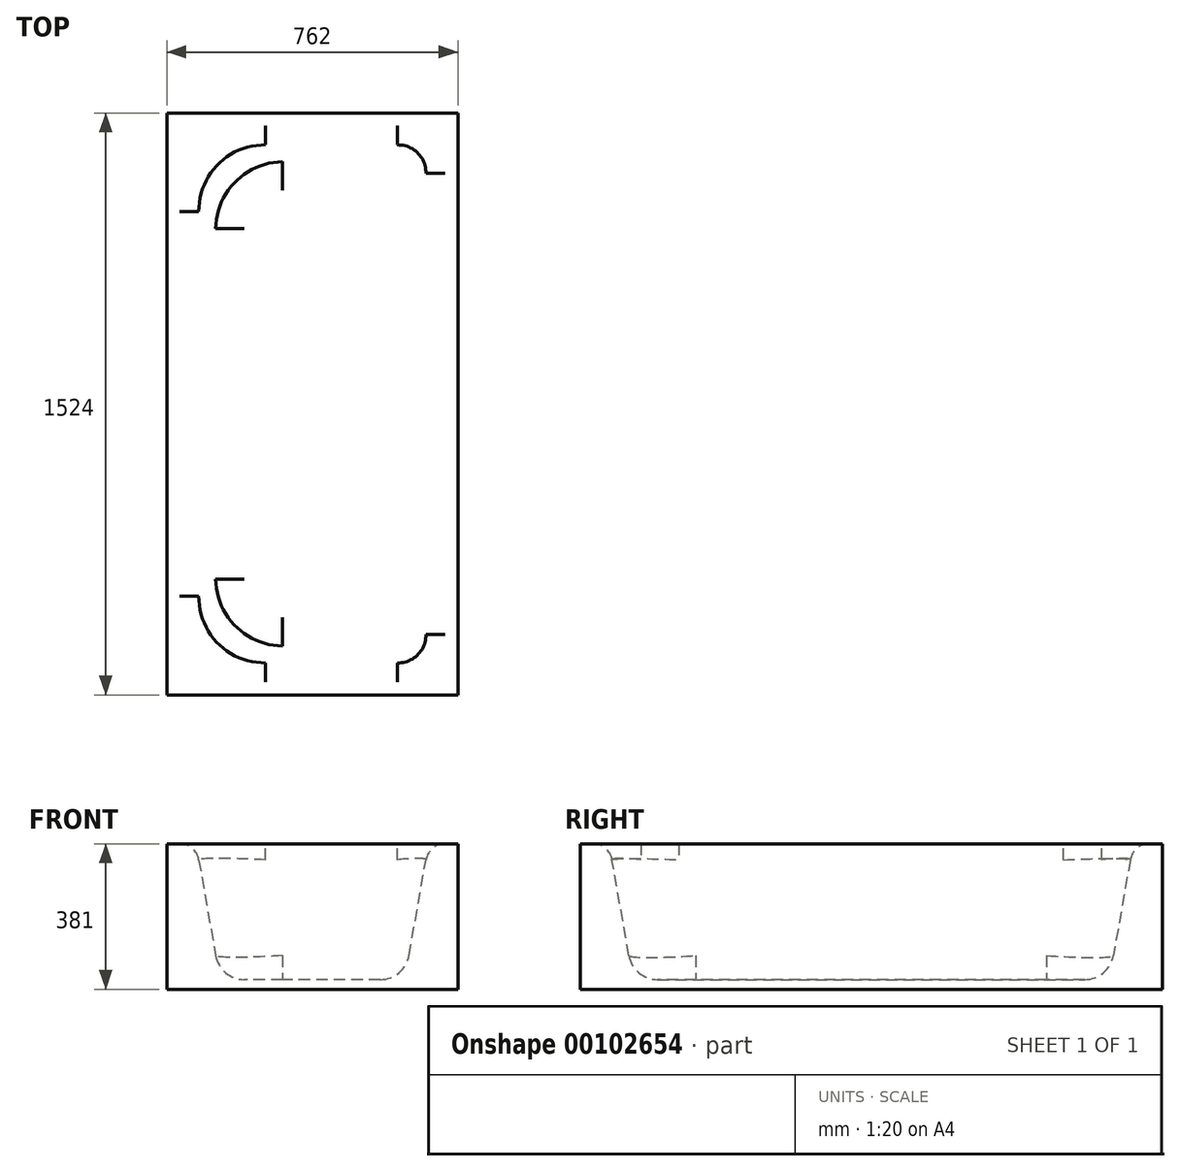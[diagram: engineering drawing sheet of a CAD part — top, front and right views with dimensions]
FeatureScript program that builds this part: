
annotation { "Feature Type Name" : "Feature", "Feature Type Description" : "" }
export const myFeature = defineFeature(function(context is Context, id is Id, definition is map)
    precondition{}
    {
        {
            var Q0;
            Q0=qCreatedBy(makeId("Top.planeOp"),FACE);
            var sketch = newSketch(context, id + "F0", { "sketchPlane" : qUnion([Q0])});
            skLineSegment(sketch, "E0.bottom", {"start": v(0, 0) * mm, "end": v(762, 0) * mm});
            skLineSegment(sketch, "E0.top", {"start": v(0, 1524) * mm, "end": v(762, 1524) * mm});
            skLineSegment(sketch, "E0.left", {"start": v(0, 0) * mm, "end": v(0, 1524) * mm});
            skLineSegment(sketch, "E0.right", {"start": v(762, 0) * mm, "end": v(762, 1524) * mm});
            skSolve(sketch);
        }
        {
            var Q0;
            Q0 = qSketchRegion(id + "F0", true);
            extrude(context, id + "F1", {"entities" : qUnion([Q0]), "depth" : 381 * mm});
        }
        {
            var Q0;
            Q0=makeQuery(id+"F1.opExtrude","CAP_FACE",FACE,{"disambiguationData":[OSD([sQuery(id+"F0.wireOp",EDGE,"E0.bottom"),sQuery(id+"F0.wireOp",EDGE,"E0.top"),sQuery(id+"F0.wireOp",EDGE,"E0.left"),sQuery(id+"F0.wireOp",EDGE,"E0.right")])],"isStart":false});
            var sketch = newSketch(context, id + "F2", { "sketchPlane" : qUnion([Q0])});
            skLineSegment(sketch, "E1.bottom", {"start": v(76.2, 1447.8) * mm, "end": v(685.8, 1447.8) * mm});
            skLineSegment(sketch, "E1.top", {"start": v(76.2, 76.2) * mm, "end": v(685.8, 76.2) * mm});
            skLineSegment(sketch, "E1.left", {"start": v(76.2, 1447.8) * mm, "end": v(76.2, 76.2) * mm});
            skLineSegment(sketch, "E1.right", {"start": v(685.8, 1447.8) * mm, "end": v(685.8, 76.2) * mm});
            skSolve(sketch);
        }
        {
            var Q0;
            Q0 = qSketchRegion(id + "F2", true);
            extrude(context, id + "F3", {"entities" : qUnion([Q0]), "operationType" : NewBodyOperationType.REMOVE, "oppositeDirection" : true, "depth" : 355.6 * mm, "hasDraft" : true, "draftAngle" : 10 * degree, "draftPullDirection" : true});
        }
        {
            var Q0;
            Q0=makeQuery(id+"F3.boolean.opBoolean","COPY",EDGE,{"derivedFrom":makeQuery(id+"F3.opExtrude","SWEPT_EDGE",EDGE,{"disambiguationData":[OSD([sQuery(id+"F2.wireOp",EDGE,"E1.bottom"),sQuery(id+"F2.wireOp",EDGE,"E1.left")])]})});
            var Q1;
            Q1=makeQuery(id+"F3.boolean.opBoolean","COPY",EDGE,{"derivedFrom":makeQuery(id+"F3.opExtrude","SWEPT_EDGE",EDGE,{"disambiguationData":[OSD([sQuery(id+"F2.wireOp",EDGE,"E1.top"),sQuery(id+"F2.wireOp",EDGE,"E1.left")])]})});
            fillet(context, id + "F4", {"entities" : qUnion([Q0, Q1]), "radius" : 177.8 * mm, "tangentPropagation" : true, "allowEdgeOverflow" : false});
        }
        {
            var Q0;
            Q0=makeQuery(id+"F3.boolean.opBoolean","COPY",EDGE,{"derivedFrom":makeQuery(id+"F3.opExtrude","SWEPT_EDGE",EDGE,{"disambiguationData":[OSD([sQuery(id+"F2.wireOp",EDGE,"E1.bottom"),sQuery(id+"F2.wireOp",EDGE,"E1.right")])]})});
            var Q1;
            Q1=makeQuery(id+"F3.boolean.opBoolean","COPY",EDGE,{"derivedFrom":makeQuery(id+"F3.opExtrude","SWEPT_EDGE",EDGE,{"disambiguationData":[OSD([sQuery(id+"F2.wireOp",EDGE,"E1.top"),sQuery(id+"F2.wireOp",EDGE,"E1.right")])]})});
            fillet(context, id + "F5", {"entities" : qUnion([Q0, Q1]), "radius" : 76.2 * mm, "tangentPropagation" : true, "allowEdgeOverflow" : false});
        }
        {
            var Q0;
            {var subQ0=sQuery(id+"F2.wireOp",EDGE,"E1.left");var subQ1=sQuery(id+"F2.wireOp",EDGE,"E1.bottom");Q0=makeQuery(id+"F4.opFillet","BLEND_EDGE",EDGE,{"blendedFrom":[makeQuery(id+"F3.boolean.opBoolean","COPY",EDGE,{"derivedFrom":makeQuery(id+"F3.opExtrude","SWEPT_EDGE",EDGE,{"disambiguationData":[OSD([subQ1,subQ0])]})}),makeQuery(id+"F3.boolean.opBoolean","COPY",FACE,{"derivedFrom":makeQuery(id+"F3.opExtrude","CAP_FACE",FACE,{"disambiguationData":[OSD([subQ1,sQuery(id+"F2.wireOp",EDGE,"E1.top"),subQ0,sQuery(id+"F2.wireOp",EDGE,"E1.right")])],"isStart":false})})],"blendedInto":[makeQuery(id+"F3.boolean.opBoolean","COPY",FACE,{"derivedFrom":makeQuery(id+"F3.opExtrude","CAP_FACE",FACE,{"disambiguationData":[OSD([subQ1,sQuery(id+"F2.wireOp",EDGE,"E1.top"),subQ0,sQuery(id+"F2.wireOp",EDGE,"E1.right")])],"isStart":false})})]});}
            var Q1;
            Q1=makeQuery(id+"F3.boolean.opBoolean","COPY",EDGE,{"derivedFrom":makeQuery(id+"F3.opExtrude","CAP_EDGE",EDGE,{"disambiguationData":[OSD([sQuery(id+"F2.wireOp",EDGE,"E1.bottom")])],"isStart":false})});
            var Q2;
            {var subQ0=sQuery(id+"F2.wireOp",EDGE,"E1.right");var subQ1=sQuery(id+"F2.wireOp",EDGE,"E1.bottom");Q2=makeQuery(id+"F5.opFillet","BLEND_EDGE",EDGE,{"blendedFrom":[makeQuery(id+"F3.boolean.opBoolean","COPY",EDGE,{"derivedFrom":makeQuery(id+"F3.opExtrude","SWEPT_EDGE",EDGE,{"disambiguationData":[OSD([subQ1,subQ0])]})}),makeQuery(id+"F3.boolean.opBoolean","COPY",FACE,{"derivedFrom":makeQuery(id+"F3.opExtrude","CAP_FACE",FACE,{"disambiguationData":[OSD([subQ1,sQuery(id+"F2.wireOp",EDGE,"E1.top"),sQuery(id+"F2.wireOp",EDGE,"E1.left"),subQ0])],"isStart":false})})],"blendedInto":[makeQuery(id+"F3.boolean.opBoolean","COPY",FACE,{"derivedFrom":makeQuery(id+"F3.opExtrude","CAP_FACE",FACE,{"disambiguationData":[OSD([subQ1,sQuery(id+"F2.wireOp",EDGE,"E1.top"),sQuery(id+"F2.wireOp",EDGE,"E1.left"),subQ0])],"isStart":false})})]});}
            var Q3;
            {var subQ0=sQuery(id+"F2.wireOp",EDGE,"E1.right");var subQ1=sQuery(id+"F2.wireOp",EDGE,"E1.top");Q3=makeQuery(id+"F5.opFillet","BLEND_EDGE",EDGE,{"blendedFrom":[makeQuery(id+"F3.boolean.opBoolean","COPY",EDGE,{"derivedFrom":makeQuery(id+"F3.opExtrude","SWEPT_EDGE",EDGE,{"disambiguationData":[OSD([subQ1,subQ0])]})}),makeQuery(id+"F3.boolean.opBoolean","COPY",FACE,{"derivedFrom":makeQuery(id+"F3.opExtrude","CAP_FACE",FACE,{"disambiguationData":[OSD([sQuery(id+"F2.wireOp",EDGE,"E1.bottom"),subQ1,sQuery(id+"F2.wireOp",EDGE,"E1.left"),subQ0])],"isStart":false})})],"blendedInto":[makeQuery(id+"F3.boolean.opBoolean","COPY",FACE,{"derivedFrom":makeQuery(id+"F3.opExtrude","CAP_FACE",FACE,{"disambiguationData":[OSD([sQuery(id+"F2.wireOp",EDGE,"E1.bottom"),subQ1,sQuery(id+"F2.wireOp",EDGE,"E1.left"),subQ0])],"isStart":false})})]});}
            var Q4;
            Q4=makeQuery(id+"F3.boolean.opBoolean","COPY",EDGE,{"derivedFrom":makeQuery(id+"F3.opExtrude","CAP_EDGE",EDGE,{"disambiguationData":[OSD([sQuery(id+"F2.wireOp",EDGE,"E1.top")])],"isStart":false})});
            var Q5;
            {var subQ0=sQuery(id+"F2.wireOp",EDGE,"E1.left");var subQ1=sQuery(id+"F2.wireOp",EDGE,"E1.top");Q5=makeQuery(id+"F4.opFillet","BLEND_EDGE",EDGE,{"blendedFrom":[makeQuery(id+"F3.boolean.opBoolean","COPY",EDGE,{"derivedFrom":makeQuery(id+"F3.opExtrude","SWEPT_EDGE",EDGE,{"disambiguationData":[OSD([subQ1,subQ0])]})}),makeQuery(id+"F3.boolean.opBoolean","COPY",FACE,{"derivedFrom":makeQuery(id+"F3.opExtrude","CAP_FACE",FACE,{"disambiguationData":[OSD([sQuery(id+"F2.wireOp",EDGE,"E1.bottom"),subQ1,subQ0,sQuery(id+"F2.wireOp",EDGE,"E1.right")])],"isStart":false})})],"blendedInto":[makeQuery(id+"F3.boolean.opBoolean","COPY",FACE,{"derivedFrom":makeQuery(id+"F3.opExtrude","CAP_FACE",FACE,{"disambiguationData":[OSD([sQuery(id+"F2.wireOp",EDGE,"E1.bottom"),subQ1,subQ0,sQuery(id+"F2.wireOp",EDGE,"E1.right")])],"isStart":false})})]});}
            var Q6;
            Q6=makeQuery(id+"F3.boolean.opBoolean","COPY",EDGE,{"derivedFrom":makeQuery(id+"F3.opExtrude","CAP_EDGE",EDGE,{"disambiguationData":[OSD([sQuery(id+"F2.wireOp",EDGE,"E1.left")])],"isStart":false})});
            var Q7;
            Q7=makeQuery(id+"F3.boolean.opBoolean","COPY",EDGE,{"derivedFrom":makeQuery(id+"F3.opExtrude","CAP_EDGE",EDGE,{"disambiguationData":[OSD([sQuery(id+"F2.wireOp",EDGE,"E1.right")])],"isStart":false})});
            fillet(context, id + "F6", {"entities" : qUnion([Q0, Q1, Q2, Q3, Q4, Q5, Q6, Q7]), "radius" : 76.2 * mm, "tangentPropagation" : true, "allowEdgeOverflow" : false});
        }
        {
            var Q0;
            Q0=makeQuery(id+"F4.opFillet","BLEND_EDGE",EDGE,{"blendedFrom":[makeQuery(id+"F3.boolean.opBoolean","COPY",EDGE,{"derivedFrom":makeQuery(id+"F3.opExtrude","SWEPT_EDGE",EDGE,{"disambiguationData":[OSD([sQuery(id+"F2.wireOp",EDGE,"E1.bottom"),sQuery(id+"F2.wireOp",EDGE,"E1.left")])]})}),makeQuery(id+"F1.opExtrude","CAP_FACE",FACE,{"disambiguationData":[OSD([sQuery(id+"F0.wireOp",EDGE,"E0.bottom"),sQuery(id+"F0.wireOp",EDGE,"E0.top"),sQuery(id+"F0.wireOp",EDGE,"E0.left"),sQuery(id+"F0.wireOp",EDGE,"E0.right")])],"isStart":false})],"blendedInto":[makeQuery(id+"F1.opExtrude","CAP_FACE",FACE,{"disambiguationData":[OSD([sQuery(id+"F0.wireOp",EDGE,"E0.bottom"),sQuery(id+"F0.wireOp",EDGE,"E0.top"),sQuery(id+"F0.wireOp",EDGE,"E0.left"),sQuery(id+"F0.wireOp",EDGE,"E0.right")])],"isStart":false})]});
            var Q1;
            Q1=makeQuery(id+"F3.boolean.opBoolean","COPY",EDGE,{"derivedFrom":makeQuery(id+"F3.opExtrude","CAP_EDGE",EDGE,{"disambiguationData":[OSD([sQuery(id+"F2.wireOp",EDGE,"E1.left")])],"isStart":true})});
            var Q2;
            Q2=makeQuery(id+"F4.opFillet","BLEND_EDGE",EDGE,{"blendedFrom":[makeQuery(id+"F3.boolean.opBoolean","COPY",EDGE,{"derivedFrom":makeQuery(id+"F3.opExtrude","SWEPT_EDGE",EDGE,{"disambiguationData":[OSD([sQuery(id+"F2.wireOp",EDGE,"E1.top"),sQuery(id+"F2.wireOp",EDGE,"E1.left")])]})}),makeQuery(id+"F1.opExtrude","CAP_FACE",FACE,{"disambiguationData":[OSD([sQuery(id+"F0.wireOp",EDGE,"E0.bottom"),sQuery(id+"F0.wireOp",EDGE,"E0.top"),sQuery(id+"F0.wireOp",EDGE,"E0.left"),sQuery(id+"F0.wireOp",EDGE,"E0.right")])],"isStart":false})],"blendedInto":[makeQuery(id+"F1.opExtrude","CAP_FACE",FACE,{"disambiguationData":[OSD([sQuery(id+"F0.wireOp",EDGE,"E0.bottom"),sQuery(id+"F0.wireOp",EDGE,"E0.top"),sQuery(id+"F0.wireOp",EDGE,"E0.left"),sQuery(id+"F0.wireOp",EDGE,"E0.right")])],"isStart":false})]});
            var Q3;
            Q3=makeQuery(id+"F3.boolean.opBoolean","COPY",EDGE,{"derivedFrom":makeQuery(id+"F3.opExtrude","CAP_EDGE",EDGE,{"disambiguationData":[OSD([sQuery(id+"F2.wireOp",EDGE,"E1.top")])],"isStart":true})});
            var Q4;
            Q4=makeQuery(id+"F5.opFillet","BLEND_EDGE",EDGE,{"blendedFrom":[makeQuery(id+"F3.boolean.opBoolean","COPY",EDGE,{"derivedFrom":makeQuery(id+"F3.opExtrude","SWEPT_EDGE",EDGE,{"disambiguationData":[OSD([sQuery(id+"F2.wireOp",EDGE,"E1.top"),sQuery(id+"F2.wireOp",EDGE,"E1.right")])]})}),makeQuery(id+"F1.opExtrude","CAP_FACE",FACE,{"disambiguationData":[OSD([sQuery(id+"F0.wireOp",EDGE,"E0.bottom"),sQuery(id+"F0.wireOp",EDGE,"E0.top"),sQuery(id+"F0.wireOp",EDGE,"E0.left"),sQuery(id+"F0.wireOp",EDGE,"E0.right")])],"isStart":false})],"blendedInto":[makeQuery(id+"F1.opExtrude","CAP_FACE",FACE,{"disambiguationData":[OSD([sQuery(id+"F0.wireOp",EDGE,"E0.bottom"),sQuery(id+"F0.wireOp",EDGE,"E0.top"),sQuery(id+"F0.wireOp",EDGE,"E0.left"),sQuery(id+"F0.wireOp",EDGE,"E0.right")])],"isStart":false})]});
            var Q5;
            Q5=makeQuery(id+"F3.boolean.opBoolean","COPY",EDGE,{"derivedFrom":makeQuery(id+"F3.opExtrude","CAP_EDGE",EDGE,{"disambiguationData":[OSD([sQuery(id+"F2.wireOp",EDGE,"E1.right")])],"isStart":true})});
            var Q6;
            Q6=makeQuery(id+"F5.opFillet","BLEND_EDGE",EDGE,{"blendedFrom":[makeQuery(id+"F3.boolean.opBoolean","COPY",EDGE,{"derivedFrom":makeQuery(id+"F3.opExtrude","SWEPT_EDGE",EDGE,{"disambiguationData":[OSD([sQuery(id+"F2.wireOp",EDGE,"E1.bottom"),sQuery(id+"F2.wireOp",EDGE,"E1.right")])]})}),makeQuery(id+"F1.opExtrude","CAP_FACE",FACE,{"disambiguationData":[OSD([sQuery(id+"F0.wireOp",EDGE,"E0.bottom"),sQuery(id+"F0.wireOp",EDGE,"E0.top"),sQuery(id+"F0.wireOp",EDGE,"E0.left"),sQuery(id+"F0.wireOp",EDGE,"E0.right")])],"isStart":false})],"blendedInto":[makeQuery(id+"F1.opExtrude","CAP_FACE",FACE,{"disambiguationData":[OSD([sQuery(id+"F0.wireOp",EDGE,"E0.bottom"),sQuery(id+"F0.wireOp",EDGE,"E0.top"),sQuery(id+"F0.wireOp",EDGE,"E0.left"),sQuery(id+"F0.wireOp",EDGE,"E0.right")])],"isStart":false})]});
            var Q7;
            Q7=makeQuery(id+"F3.boolean.opBoolean","COPY",EDGE,{"derivedFrom":makeQuery(id+"F3.opExtrude","CAP_EDGE",EDGE,{"disambiguationData":[OSD([sQuery(id+"F2.wireOp",EDGE,"E1.bottom")])],"isStart":true})});
            fillet(context, id + "F7", {"entities" : qUnion([Q0, Q1, Q2, Q3, Q4, Q5, Q6, Q7]), "radius" : 50.8 * mm, "tangentPropagation" : true, "allowEdgeOverflow" : false});
        }
    });
